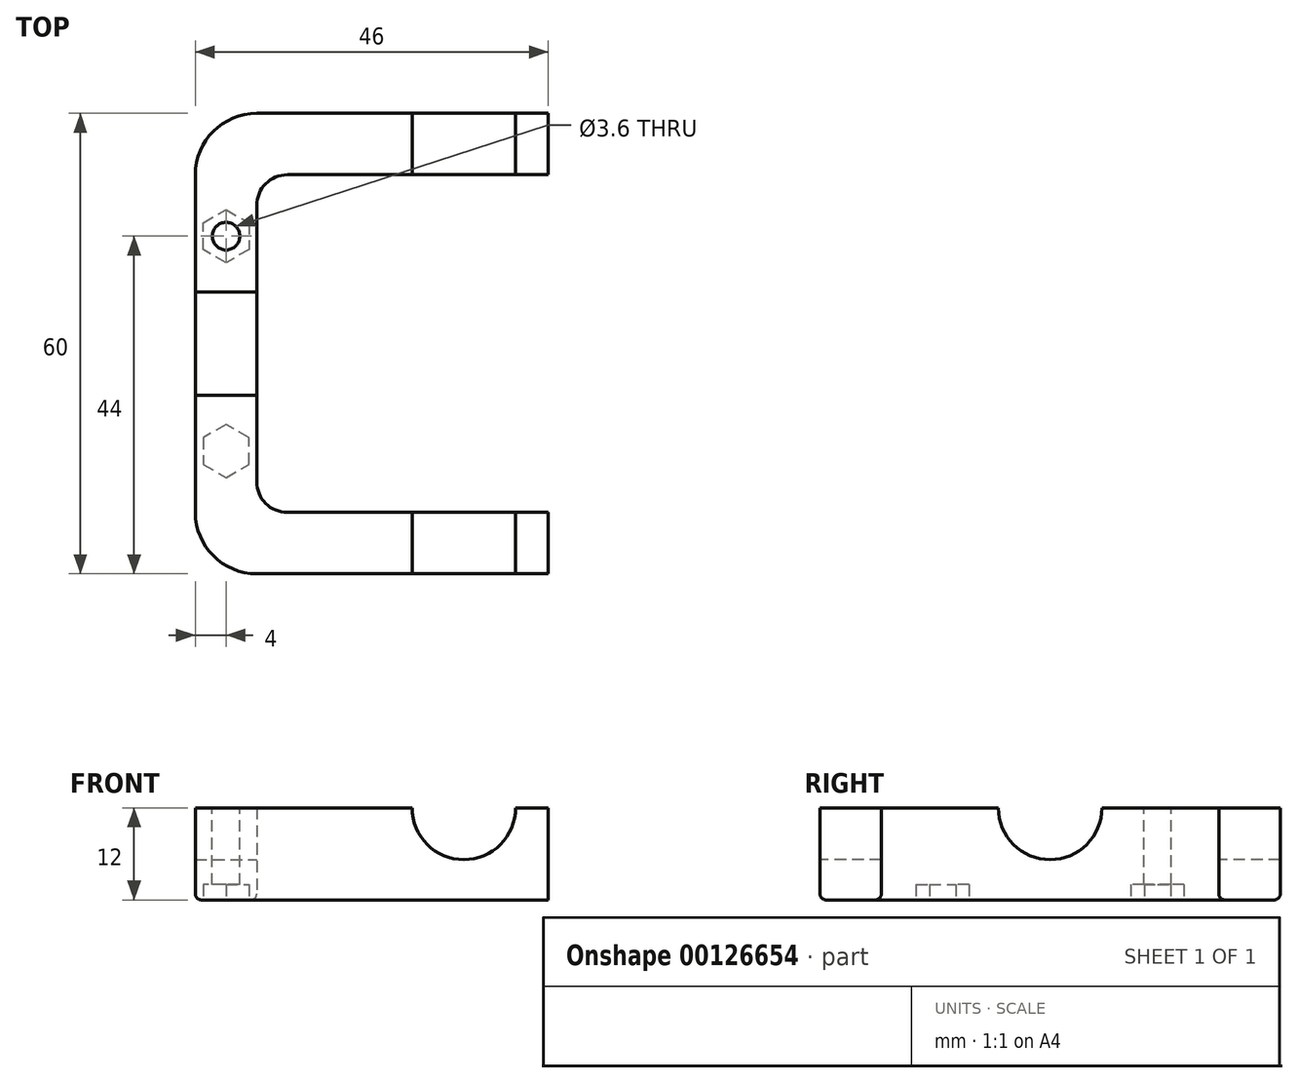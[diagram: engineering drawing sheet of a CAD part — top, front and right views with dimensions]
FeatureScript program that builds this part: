
annotation { "Feature Type Name" : "Feature", "Feature Type Description" : "" }
export const myFeature = defineFeature(function(context is Context, id is Id, definition is map)
    precondition{}
    {
        {
            var Q0;
            Q0=qCreatedBy(makeId("Top.planeOp"),FACE);
            var sketch = newSketch(context, id + "F0", { "sketchPlane" : qUnion([Q0])});
            skLineSegment(sketch, "E0.bottom", {"start": v(-30, 30) * mm, "end": v(30, 30) * mm});
            skLineSegment(sketch, "E0.top", {"start": v(-30, -30) * mm, "end": v(30, -30) * mm});
            skLineSegment(sketch, "E0.left", {"start": v(-30, 30) * mm, "end": v(-30, -30) * mm});
            skLineSegment(sketch, "E0.right", {"start": v(30, 30) * mm, "end": v(30, -30) * mm});
            skLineSegment(sketch, "E1", {"start": v(0, 30) * mm, "end": v(0, -30) * mm, "construction": true});
            skLineSegment(sketch, "E2", {"start": v(-30, 0) * mm, "end": v(30, 0) * mm, "construction": true});
            skLineSegment(sketch, "E3.bottom", {"start": v(-22, 22) * mm, "end": v(22, 22) * mm});
            skLineSegment(sketch, "E3.top", {"start": v(-22, -22) * mm, "end": v(22, -22) * mm});
            skLineSegment(sketch, "E3.left", {"start": v(-22, 22) * mm, "end": v(-22, -22) * mm});
            skLineSegment(sketch, "E3.right", {"start": v(22, 22) * mm, "end": v(22, -22) * mm});
            skLineSegment(sketch, "E4", {"start": v(0, 22) * mm, "end": v(0, -22) * mm, "construction": true});
            skSolve(sketch);
        }
        {
            var Q0;
            Q0=makeQuery(id+"F0.imprint","IMPRINT",FACE,{"disambiguationData":[TD([[makeQuery(id+"F0.imprint","IMPRINT",EDGE,{"derivedFrom":sQuery(id+"F0.wireOp",EDGE,"TTZx1SDF-Yl1d-4XTd-kP7O-AWufJlUFJuJy")}),-1.0]])]});
            var Q1;
            Q1=makeQuery(id+"F0.imprint","IMPRINT",FACE,{"disambiguationData":[TD([[makeQuery(id+"F0.imprint","IMPRINT",EDGE,{"derivedFrom":sQuery(id+"F0.wireOp",EDGE,"E0.bottom")}),-1.0]])]});
            extrude(context, id + "F1", {"entities" : qUnion([Q0, Q1]), "depth" : 12 * mm});
        }
        {
            var Q0;
            Q0=makeQuery(id+"F1.opExtrude","CAP_FACE",FACE,{"disambiguationData":[OSD([sQuery(id+"F0.wireOp",EDGE,"E0.bottom"),sQuery(id+"F0.wireOp",EDGE,"E0.top"),sQuery(id+"F0.wireOp",EDGE,"E0.left"),sQuery(id+"F0.wireOp",EDGE,"E0.right"),sQuery(id+"F0.wireOp",EDGE,"E3.bottom"),sQuery(id+"F0.wireOp",EDGE,"E3.top"),sQuery(id+"F0.wireOp",EDGE,"E3.left"),sQuery(id+"F0.wireOp",EDGE,"E3.right")])],"isStart":false});
            var sketch = newSketch(context, id + "F2", { "sketchPlane" : qUnion([Q0])});
            skLineSegment(sketch, "E5.bottom", {"start": v(30, 30) * mm, "end": v(16, 30) * mm});
            skLineSegment(sketch, "E5.top", {"start": v(30, -30) * mm, "end": v(16, -30) * mm});
            skLineSegment(sketch, "E5.left", {"start": v(30, 30) * mm, "end": v(30, -30) * mm});
            skLineSegment(sketch, "E5.right", {"start": v(16, 30) * mm, "end": v(16, -30) * mm});
            skSolve(sketch);
        }
        {
            var Q0;
            {var subQ1=sQuery(id+"F2.wireOp",EDGE,"E5.bottom");Q0=makeQuery(id+"F2.imprint","IMPRINT",FACE,{"disambiguationData":[TD([[makeQuery(id+"F2.imprint","IMPRINT",EDGE,{"derivedFrom":subQ1}),-1.0]])]});}
            extrude(context, id + "F3", {"entities" : qUnion([Q0]), "operationType" : NewBodyOperationType.REMOVE, "oppositeDirection" : true, "depth" : 25 * mm});
        }
        {
            var Q0;
            Q0=makeQuery(id+"F1.opExtrude","SWEPT_EDGE",EDGE,{"disambiguationData":[OSD([sQuery(id+"F0.wireOp",EDGE,"E0.top"),sQuery(id+"F0.wireOp",EDGE,"E0.left")])]});
            var Q1;
            Q1=makeQuery(id+"F1.opExtrude","SWEPT_EDGE",EDGE,{"disambiguationData":[OSD([sQuery(id+"F0.wireOp",EDGE,"E0.bottom"),sQuery(id+"F0.wireOp",EDGE,"E0.left")])]});
            fillet(context, id + "F4", {"entities" : qUnion([Q0, Q1]), "radius" : 8 * mm, "tangentPropagation" : true, "allowEdgeOverflow" : false});
        }
        {
            var Q0;
            Q0=makeQuery(id+"F1.opExtrude","SWEPT_EDGE",EDGE,{"disambiguationData":[OSD([sQuery(id+"F0.wireOp",EDGE,"E3.bottom"),sQuery(id+"F0.wireOp",EDGE,"E3.left")])]});
            var Q1;
            Q1=makeQuery(id+"F1.opExtrude","SWEPT_EDGE",EDGE,{"disambiguationData":[OSD([sQuery(id+"F0.wireOp",EDGE,"E3.top"),sQuery(id+"F0.wireOp",EDGE,"E3.left")])]});
            fillet(context, id + "F5", {"entities" : qUnion([Q0, Q1]), "radius" : 4 * mm, "tangentPropagation" : true, "allowEdgeOverflow" : false});
        }
        {
            var Q0;
            Q0=makeQuery(id+"F1.opExtrude","SWEPT_FACE",FACE,{"disambiguationData":[OSD([sQuery(id+"F0.wireOp",EDGE,"E3.left")])]});
            var sketch = newSketch(context, id + "F6", { "sketchPlane" : qUnion([Q0])});
            skCircle(sketch, "E6", {"center": v(0, 12) * mm, "radius": 6.75 * mm});
            skSolve(sketch);
        }
        {
            var Q0;
            {var subQ0=sQuery(id+"F6.wireOp",EDGE,"E6");var subQ1=makeQuery(id+"F1.opExtrude","CAP_EDGE",EDGE,{"disambiguationData":[OSD([sQuery(id+"F0.wireOp",EDGE,"E3.left")])],"isStart":false});var subQ2=makeQuery(id+"F6.imprint","INTERSECT",VERTEX,{"disambiguationData":[OD(0.0)],"derivedFrom":[subQ1,subQ0]});Q0=makeQuery(id+"F6.imprint","IMPRINT",FACE,{"disambiguationData":[TD([[makeQuery(id+"F6.imprint","IMPRINT",EDGE,{"disambiguationData":[TD([[subQ2,1.0]])],"derivedFrom":subQ0}),1.0]])]});}
            extrude(context, id + "F7", {"entities" : qUnion([Q0]), "operationType" : NewBodyOperationType.REMOVE, "oppositeDirection" : true, "depth" : 25 * mm});
        }
        {
            var Q0;
            Q0=makeQuery(id+"F1.opExtrude","SWEPT_FACE",FACE,{"disambiguationData":[OSD([sQuery(id+"F0.wireOp",EDGE,"E0.top")])]});
            var sketch = newSketch(context, id + "F8", { "sketchPlane" : qUnion([Q0])});
            skCircle(sketch, "E7", {"center": v(5, 12) * mm, "radius": 6.75 * mm});
            skSolve(sketch);
        }
        {
            var Q0;
            {var subQ0=sQuery(id+"F8.wireOp",EDGE,"E7");var subQ1=makeQuery(id+"F1.opExtrude","CAP_EDGE",EDGE,{"disambiguationData":[OSD([sQuery(id+"F0.wireOp",EDGE,"E0.top")])],"isStart":false});var subQ2=makeQuery(id+"F8.imprint","INTERSECT",VERTEX,{"disambiguationData":[OD(0.0)],"derivedFrom":[subQ1,subQ0]});Q0=makeQuery(id+"F8.imprint","IMPRINT",FACE,{"disambiguationData":[TD([[makeQuery(id+"F8.imprint","IMPRINT",EDGE,{"disambiguationData":[TD([[subQ2,1.0]])],"derivedFrom":subQ0}),1.0]])]});}
            extrude(context, id + "F9", {"entities" : qUnion([Q0]), "operationType" : NewBodyOperationType.REMOVE, "endBound" : BoundingType.THROUGH_ALL, "oppositeDirection" : true, "depth" : 25 * mm});
        }
        {
            var Q0;
            {var subQ0=sQuery(id+"F0.wireOp",EDGE,"E3.left");var subQ2=sQuery(id+"F0.wireOp",EDGE,"E3.bottom");var subQ4=sQuery(id+"F0.wireOp",EDGE,"E0.left");var subQ5=makeQuery(id+"F1.opExtrude","SWEPT_FACE",FACE,{"disambiguationData":[OSD([subQ4])]});var subQ6=sQuery(id+"F0.wireOp",EDGE,"E0.bottom");var subQ8=makeQuery(id+"F1.opExtrude","SWEPT_FACE",FACE,{"disambiguationData":[OSD([subQ6])]});Q0=makeQuery(id+"F9.boolean.opBoolean","SPLIT",FACE,{"disambiguationData":[TD([subQ5])],"derivedFrom":makeQuery(id+"F7.boolean.opBoolean","SPLIT",FACE,{"disambiguationData":[TD([subQ8])],"derivedFrom":makeQuery(id+"F1.opExtrude","CAP_FACE",FACE,{"disambiguationData":[OSD([subQ6,sQuery(id+"F0.wireOp",EDGE,"E0.top"),subQ4,sQuery(id+"F0.wireOp",EDGE,"E0.right"),subQ2,sQuery(id+"F0.wireOp",EDGE,"E3.top"),subQ0,sQuery(id+"F0.wireOp",EDGE,"E3.right")])],"isStart":false})})});}
            var sketch = newSketch(context, id + "F10", { "sketchPlane" : qUnion([Q0])});
            skCircle(sketch, "E8", {"center": v(-26, 14) * mm, "radius": 1.8 * mm});
            skLineSegment(sketch, "E9", {"start": v(-19.25, 0) * mm, "end": v(-36.62, 0) * mm, "construction": true});
            skLineSegment(sketch, "E10", {"start": v(-30, 14) * mm, "end": v(-22, 14) * mm, "construction": true});
            skCircle(sketch, "E11.MirrorC", {"center": v(-26, -14) * mm, "radius": 1.8 * mm});
            skSolve(sketch);
        }
        {
            var Q0;
            Q0=makeQuery(id+"F10.imprint","IMPRINT",FACE,{"disambiguationData":[TD([[makeQuery(id+"F10.imprint","IMPRINT",EDGE,{"derivedFrom":sQuery(id+"F10.wireOp",EDGE,"E8")}),1.0]])]});
            var Q1;
            Q1=makeQuery(id+"F10.imprint","IMPRINT",FACE,{"disambiguationData":[TD([[makeQuery(id+"F10.imprint","IMPRINT",EDGE,{"derivedFrom":sQuery(id+"F10.wireOp",EDGE,"E11.MirrorC")}),-1.0]])]});
            extrude(context, id + "F11", {"entities" : qUnion([Q0, Q1]), "operationType" : NewBodyOperationType.REMOVE, "oppositeDirection" : true, "depth" : 25 * mm});
        }
        {
            var Q0;
            Q0=makeQuery(id+"F1.opExtrude","CAP_EDGE",EDGE,{"disambiguationData":[OSD([sQuery(id+"F0.wireOp",EDGE,"E0.top")])],"isStart":true});
            var Q1;
            {var subQ0=sQuery(id+"F0.wireOp",EDGE,"E3.left");var subQ1=sQuery(id+"F0.wireOp",EDGE,"E3.bottom");Q1=makeQuery(id+"F5.opFillet","BLEND_EDGE",EDGE,{"blendedFrom":[makeQuery(id+"F1.opExtrude","SWEPT_EDGE",EDGE,{"disambiguationData":[OSD([subQ1,subQ0])]}),makeQuery(id+"F1.opExtrude","CAP_FACE",FACE,{"disambiguationData":[OSD([sQuery(id+"F0.wireOp",EDGE,"E0.bottom"),sQuery(id+"F0.wireOp",EDGE,"E0.top"),sQuery(id+"F0.wireOp",EDGE,"E0.left"),sQuery(id+"F0.wireOp",EDGE,"E0.right"),subQ1,sQuery(id+"F0.wireOp",EDGE,"E3.top"),subQ0,sQuery(id+"F0.wireOp",EDGE,"E3.right")])],"isStart":true})],"blendedInto":[makeQuery(id+"F1.opExtrude","CAP_FACE",FACE,{"disambiguationData":[OSD([sQuery(id+"F0.wireOp",EDGE,"E0.bottom"),sQuery(id+"F0.wireOp",EDGE,"E0.top"),sQuery(id+"F0.wireOp",EDGE,"E0.left"),sQuery(id+"F0.wireOp",EDGE,"E0.right"),subQ1,sQuery(id+"F0.wireOp",EDGE,"E3.top"),subQ0,sQuery(id+"F0.wireOp",EDGE,"E3.right")])],"isStart":true})]});}
            fillet(context, id + "F12", {"entities" : qUnion([Q0, Q1]), "radius" : 0.8 * mm, "tangentPropagation" : true, "allowEdgeOverflow" : false});
        }
        {
            var Q0;
            Q0=makeQuery(id+"F1.opExtrude","CAP_FACE",FACE,{"disambiguationData":[OSD([sQuery(id+"F0.wireOp",EDGE,"E0.bottom"),sQuery(id+"F0.wireOp",EDGE,"E0.top"),sQuery(id+"F0.wireOp",EDGE,"E0.left"),sQuery(id+"F0.wireOp",EDGE,"E0.right"),sQuery(id+"F0.wireOp",EDGE,"E3.bottom"),sQuery(id+"F0.wireOp",EDGE,"E3.top"),sQuery(id+"F0.wireOp",EDGE,"E3.left"),sQuery(id+"F0.wireOp",EDGE,"E3.right")])],"isStart":true});
            var sketch = newSketch(context, id + "F13", { "sketchPlane" : qUnion([Q0])});
            skCircle(sketch, "E12.cCircle", {"center": v(-26, 14) * mm, "radius": 3 * mm, "construction": true});
            skLineSegment(sketch, "E12.0", {"start": v(-23, 15.73) * mm, "end": v(-23, 12.27) * mm});
            skLineSegment(sketch, "E12.1", {"start": v(-23, 12.27) * mm, "end": v(-26, 10.54) * mm});
            skLineSegment(sketch, "E12.2", {"start": v(-26, 10.54) * mm, "end": v(-29, 12.27) * mm});
            skLineSegment(sketch, "E12.3", {"start": v(-29, 12.27) * mm, "end": v(-29, 15.73) * mm});
            skLineSegment(sketch, "E12.4", {"start": v(-29, 15.73) * mm, "end": v(-26, 17.46) * mm});
            skLineSegment(sketch, "E12.5", {"start": v(-26, 17.46) * mm, "end": v(-23, 15.73) * mm});
            skPoint(sketch, "E12.0.midPoint", {"position": v(-23, 14) * mm});
            skPoint(sketch, "E13.MirrorP", {"position": v(-23, -14) * mm});
            skCircle(sketch, "E14.MirrorC", {"center": v(-26, -14) * mm, "radius": 3 * mm, "construction": true});
            skLineSegment(sketch, "E15.MirrorCS", {"start": v(-23, -15.73) * mm, "end": v(-23, -12.27) * mm});
            skLineSegment(sketch, "E16.MirrorCS", {"start": v(-26, -17.46) * mm, "end": v(-23, -15.73) * mm});
            skLineSegment(sketch, "E17.MirrorCS", {"start": v(-23, -12.27) * mm, "end": v(-26, -10.54) * mm});
            skLineSegment(sketch, "E18.MirrorCS", {"start": v(-26, -10.54) * mm, "end": v(-29, -12.27) * mm});
            skLineSegment(sketch, "E19.MirrorCS", {"start": v(-29, -12.27) * mm, "end": v(-29, -15.73) * mm});
            skLineSegment(sketch, "E20.MirrorCS", {"start": v(-29, -15.73) * mm, "end": v(-26, -17.46) * mm});
            skSolve(sketch);
        }
        {
            var Q0;
            Q0=makeQuery(id+"F13.imprint","IMPRINT",FACE,{"disambiguationData":[TD([[makeQuery(id+"F13.imprint","IMPRINT",EDGE,{"derivedFrom":sQuery(id+"F13.wireOp",EDGE,"E12.0")}),-1.0]])]});
            var Q1;
            Q1=makeQuery(id+"F13.imprint","IMPRINT",FACE,{"disambiguationData":[TD([[makeQuery(id+"F13.imprint","IMPRINT",EDGE,{"derivedFrom":sQuery(id+"F13.wireOp",EDGE,"E15.MirrorCS")}),1.0]])]});
            extrude(context, id + "F14", {"entities" : qUnion([Q0, Q1]), "operationType" : NewBodyOperationType.REMOVE, "oppositeDirection" : true, "depth" : 2 * mm});
        }
    });
